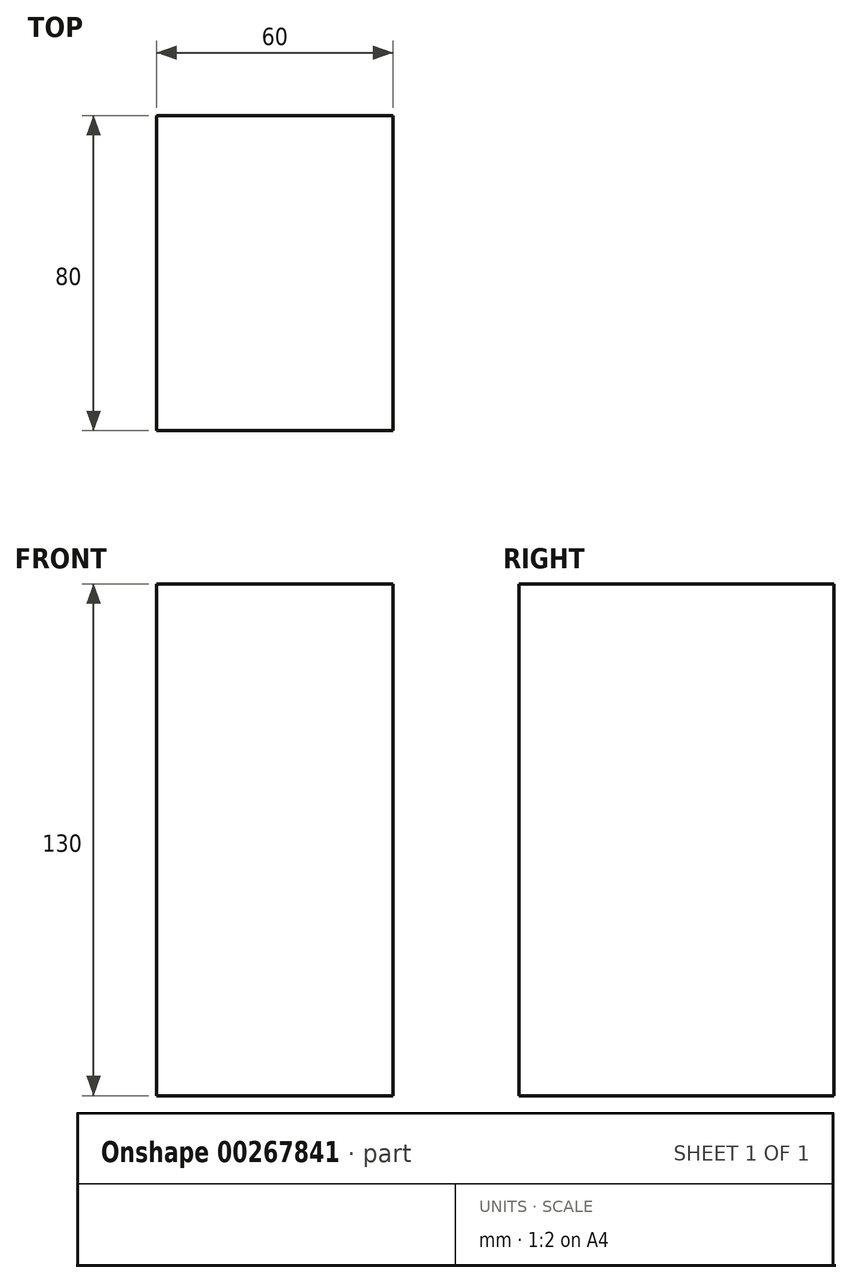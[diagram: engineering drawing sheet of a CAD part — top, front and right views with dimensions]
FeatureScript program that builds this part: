
annotation { "Feature Type Name" : "Feature", "Feature Type Description" : "" }
export const myFeature = defineFeature(function(context is Context, id is Id, definition is map)
    precondition{}
    {
        {
            var Q0;
            Q0=qCreatedBy(makeId("Top.planeOp"),FACE);
            var sketch = newSketch(context, id + "F0", { "sketchPlane" : qUnion([Q0])});
            skLineSegment(sketch, "E0.bottom", {"start": v(30, -40) * mm, "end": v(-30, -40) * mm});
            skLineSegment(sketch, "E0.top", {"start": v(30, 40) * mm, "end": v(-30, 40) * mm});
            skLineSegment(sketch, "E0.left", {"start": v(30, -40) * mm, "end": v(30, 40) * mm});
            skLineSegment(sketch, "E0.right", {"start": v(-30, -40) * mm, "end": v(-30, 40) * mm});
            skPoint(sketch, "E0.middle", {"position": v(0, 0) * mm});
            skSolve(sketch);
        }
        {
            var Q0;
            Q0=makeQuery(id+"F0.imprint","IMPRINT",FACE,{"disambiguationData":[TD([[makeQuery(id+"F0.imprint","IMPRINT",EDGE,{"derivedFrom":sQuery(id+"F0.wireOp",EDGE,"E0.bottom")}),-1.0]])]});
            extrude(context, id + "F1", {"entities" : qUnion([Q0]), "depth" : 130 * mm});
        }
    });
